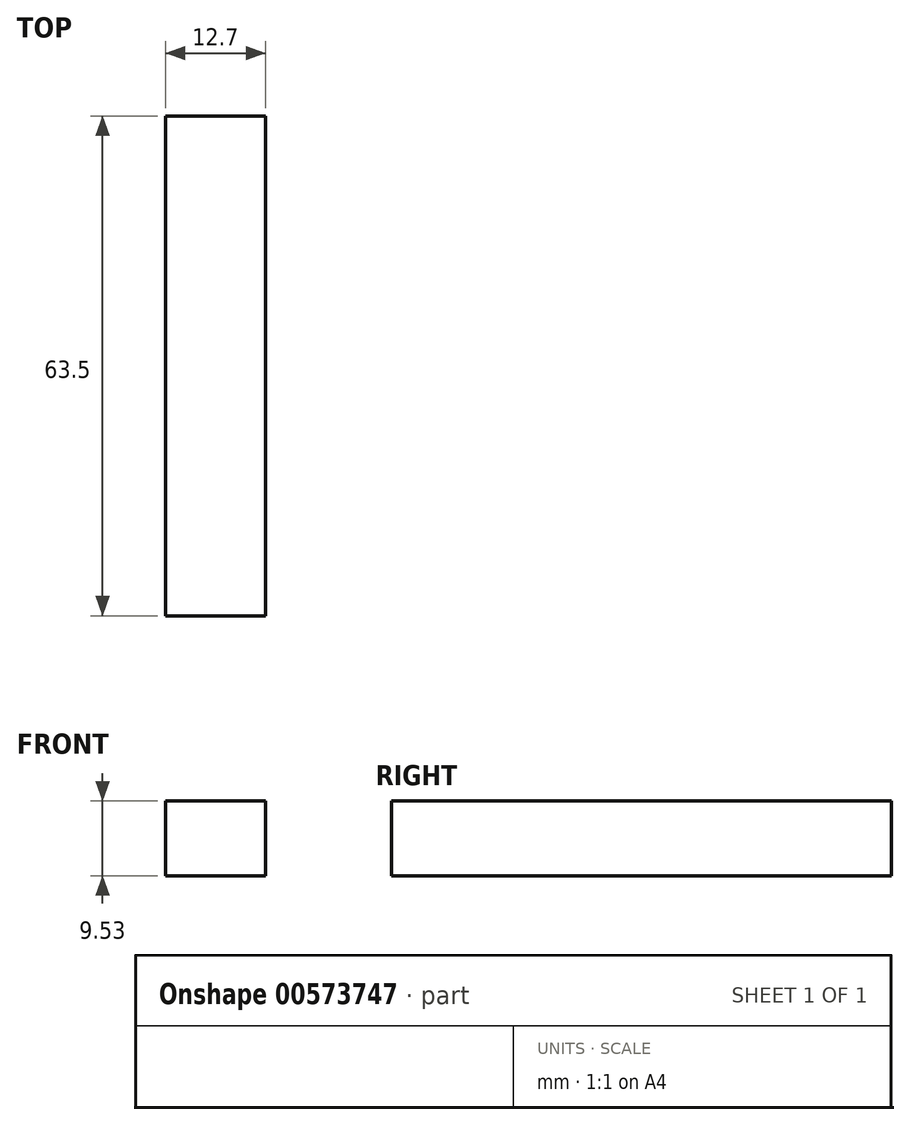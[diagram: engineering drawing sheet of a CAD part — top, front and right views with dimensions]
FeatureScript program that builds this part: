
annotation { "Feature Type Name" : "Feature", "Feature Type Description" : "" }
export const myFeature = defineFeature(function(context is Context, id is Id, definition is map)
    precondition{}
    {
        {
            var Q0;
            Q0=qCreatedBy(makeId("Top.planeOp"),FACE);
            var sketch = newSketch(context, id + "F0", { "sketchPlane" : qUnion([Q0])});
            skLineSegment(sketch, "E0.bottom", {"start": v(0, 0) * mm, "end": v(12.7, 0) * mm});
            skLineSegment(sketch, "E0.top", {"start": v(0, -63.5) * mm, "end": v(12.7, -63.5) * mm});
            skLineSegment(sketch, "E0.left", {"start": v(0, 0) * mm, "end": v(0, -63.5) * mm});
            skLineSegment(sketch, "E0.right", {"start": v(12.7, 0) * mm, "end": v(12.7, -63.5) * mm});
            skSolve(sketch);
        }
        {
            var Q0;
            Q0=makeQuery(id+"F0.imprint","IMPRINT",FACE,{"disambiguationData":[TD([[makeQuery(id+"F0.imprint","IMPRINT",EDGE,{"derivedFrom":sQuery(id+"F0.wireOp",EDGE,"E0.bottom")}),-1.0]])]});
            extrude(context, id + "F1", {"entities" : qUnion([Q0]), "depth" : 9.52 * mm, "offsetDistance" : 25.4 * mm});
        }
    });
